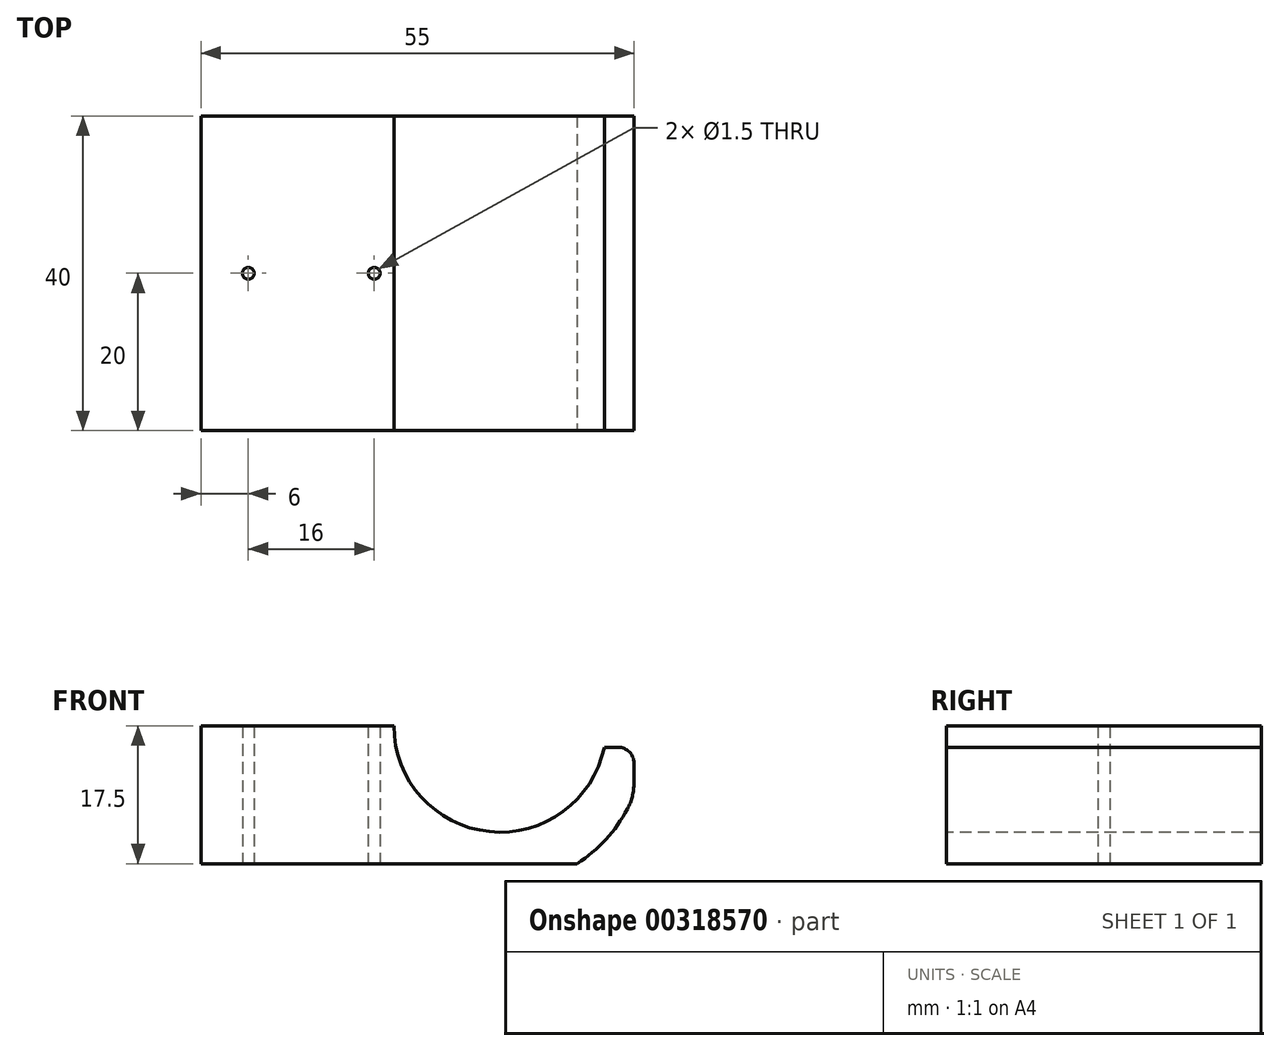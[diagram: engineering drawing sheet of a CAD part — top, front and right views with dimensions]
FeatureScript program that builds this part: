
annotation { "Feature Type Name" : "Feature", "Feature Type Description" : "" }
export const myFeature = defineFeature(function(context is Context, id is Id, definition is map)
    precondition{}
    {
        {
            var Q0;
            Q0=qCreatedBy(makeId("Top.planeOp"),FACE);
            var sketch = newSketch(context, id + "F0", { "sketchPlane" : qUnion([Q0])});
            skLineSegment(sketch, "E0.top", {"start": v(27.5, 20) * mm, "end": v(-27.5, 20) * mm});
            skLineSegment(sketch, "E0.left", {"start": v(27.5, -5) * mm, "end": v(27.5, 15) * mm});
            skLineSegment(sketch, "E0.right", {"start": v(-27.5, -20) * mm, "end": v(-27.5, 20) * mm});
            skPoint(sketch, "E0.middle", {"position": v(0, 0) * mm});
            skPoint(sketch, "E1.visualSharp", {"position": v(27.5, 20) * mm});
            skPoint(sketch, "E2.visualSharp", {"position": v(27.5, -20) * mm});
            skCircle(sketch, "E3", {"center": v(-21.5, 0) * mm, "radius": 0.75 * mm});
            skPoint(sketch, "E3.centerSnap0", {"position": v(-27.5, 0) * mm});
            skCircle(sketch, "E4", {"center": v(-5.5, 0) * mm, "radius": 0.75 * mm});
            skCircle(sketch, "E5", {"center": v(-13.5, 0) * mm, "radius": 1.25 * mm});
            skLineSegment(sketch, "E6", {"start": v(27.5, 20) * mm, "end": v(27.5, 20) * mm});
            skLineSegment(sketch, "E7", {"start": v(27.5, 15) * mm, "end": v(27.5, 20) * mm});
            skLineSegment(sketch, "E8", {"start": v(27.5, -5) * mm, "end": v(27.5, -20) * mm});
            skLineSegment(sketch, "E9", {"start": v(27.5, -20) * mm, "end": v(-27.5, -20) * mm});
            skSolve(sketch);
        }
        {
            var Q0;
            Q0=qCreatedBy(makeId("Front.planeOp"),FACE);
            var sketch = newSketch(context, id + "F1", { "sketchPlane" : qUnion([Q0])});
            skLineSegment(sketch, "E10.left", {"start": v(27.6, 0) * mm, "end": v(27.78, 17.5) * mm});
            skLineSegment(sketch, "E11", {"start": v(27.75, 14.78) * mm, "end": v(23.72, 14.78) * mm});
            skLineSegment(sketch, "E12", {"start": v(27.6, 0) * mm, "end": v(0, 0) * mm});
            skLineSegment(sketch, "E13", {"start": v(0, 0) * mm, "end": v(-3, 0) * mm});
            skLineSegment(sketch, "E14", {"start": v(-3, 0) * mm, "end": v(-3, 17.5) * mm});
            skLineSegment(sketch, "E15", {"start": v(-3, 17.5) * mm, "end": v(24, 17.5) * mm});
            skLineSegment(sketch, "E16", {"start": v(24, 17.5) * mm, "end": v(27.78, 17.5) * mm});
            skArc(sketch, "E17", {"start": v(-3, 17.5) * mm, "mid": v(10.5, 4) * mm, "end": v(24, 17.5) * mm});
            skArc(sketch, "E18", {"start": v(20.28, 0) * mm, "mid": v(24.72, 4) * mm, "end": v(27.7, 9.2) * mm});
            skSolve(sketch);
        }
        {
            var Q0;
            Q0=makeQuery(id+"F0.imprint","IMPRINT",FACE,{"disambiguationData":[TD([[makeQuery(id+"F0.imprint","IMPRINT",EDGE,{"derivedFrom":sQuery(id+"F0.wireOp",EDGE,"E0.top")}),1.0]])]});
            extrude(context, id + "F2", {"entities" : qUnion([Q0]), "depth" : 17.5 * mm});
        }
        {
            var Q0;
            Q0=makeQuery(id+"F0.imprint","IMPRINT",FACE,{"disambiguationData":[TD([[makeQuery(id+"F0.imprint","IMPRINT",EDGE,{"derivedFrom":sQuery(id+"F0.wireOp",EDGE,"E5")}),1.0]])]});
            extrude(context, id + "F3", {"entities" : qUnion([Q0]), "operationType" : NewBodyOperationType.ADD, "depth" : 17.5 * mm});
        }
        {
            var Q0;
            {var subQ0=sQuery(id+"F1.wireOp",EDGE,"E15");Q0=makeQuery(id+"F1.imprint","IMPRINT",FACE,{"disambiguationData":[TD([[makeQuery(id+"F1.imprint","IMPRINT",EDGE,{"derivedFrom":subQ0}),-1.0]])]});}
            var Q1;
            {var subQ2=sQuery(id+"F1.wireOp",EDGE,"E11");Q1=makeQuery(id+"F1.imprint","IMPRINT",FACE,{"disambiguationData":[TD([[makeQuery(id+"F1.imprint","IMPRINT",EDGE,{"derivedFrom":subQ2}),-1.0]])]});}
            var Q2;
            {var subQ3=sQuery(id+"F1.wireOp",EDGE,"E18");Q2=makeQuery(id+"F1.imprint","IMPRINT",FACE,{"disambiguationData":[TD([[makeQuery(id+"F1.imprint","IMPRINT",EDGE,{"derivedFrom":subQ3}),-1.0]])]});}
            extrude(context, id + "F4", {"entities" : qUnion([Q0, Q1, Q2]), "operationType" : NewBodyOperationType.REMOVE, "endBound" : BoundingType.SYMMETRIC, "oppositeDirection" : true, "depth" : 40 * mm});
        }
        {
            var Q0;
            Q0=makeQuery(id+"F4.boolean.opBoolean","INTERSECT",EDGE,{"derivedFrom":[makeQuery(id+"F2.opExtrude","SWEPT_FACE",FACE,{"disambiguationData":[OSD([sQuery(id+"F0.wireOp",EDGE,"E0.left"),sQuery(id+"F0.wireOp",EDGE,"E7"),sQuery(id+"F0.wireOp",EDGE,"E8")])]}),makeQuery(id+"F4.opExtrude","SWEPT_FACE",FACE,{"disambiguationData":[OSD([sQuery(id+"F1.wireOp",EDGE,"E11")])]})]});
            fillet(context, id + "F5", {"entities" : qUnion([Q0]), "radius" : 2 * mm, "tangentPropagation" : true, "allowEdgeOverflow" : false});
        }
        {
            var Q0;
            Q0=makeQuery(id+"F4.boolean.opBoolean","INTERSECT",EDGE,{"derivedFrom":[makeQuery(id+"F2.opExtrude","SWEPT_FACE",FACE,{"disambiguationData":[OSD([sQuery(id+"F0.wireOp",EDGE,"E0.left"),sQuery(id+"F0.wireOp",EDGE,"E7"),sQuery(id+"F0.wireOp",EDGE,"E8")])]}),makeQuery(id+"F4.opExtrude","SWEPT_FACE",FACE,{"disambiguationData":[OSD([sQuery(id+"F1.wireOp",EDGE,"E18")])]})]});
            var Q1;
            Q1=makeQuery(id+"F4.boolean.opBoolean","COPY",EDGE,{"derivedFrom":makeQuery(id+"F4.opExtrude","SWEPT_EDGE",EDGE,{"disambiguationData":[OSD([sQuery(id+"F1.wireOp",EDGE,"E12"),sQuery(id+"F1.wireOp",EDGE,"E18")])]})});
            fillet(context, id + "F6", {"entities" : qUnion([Q0, Q1]), "radius" : 7 * mm, "tangentPropagation" : true, "allowEdgeOverflow" : false});
        }
    });
